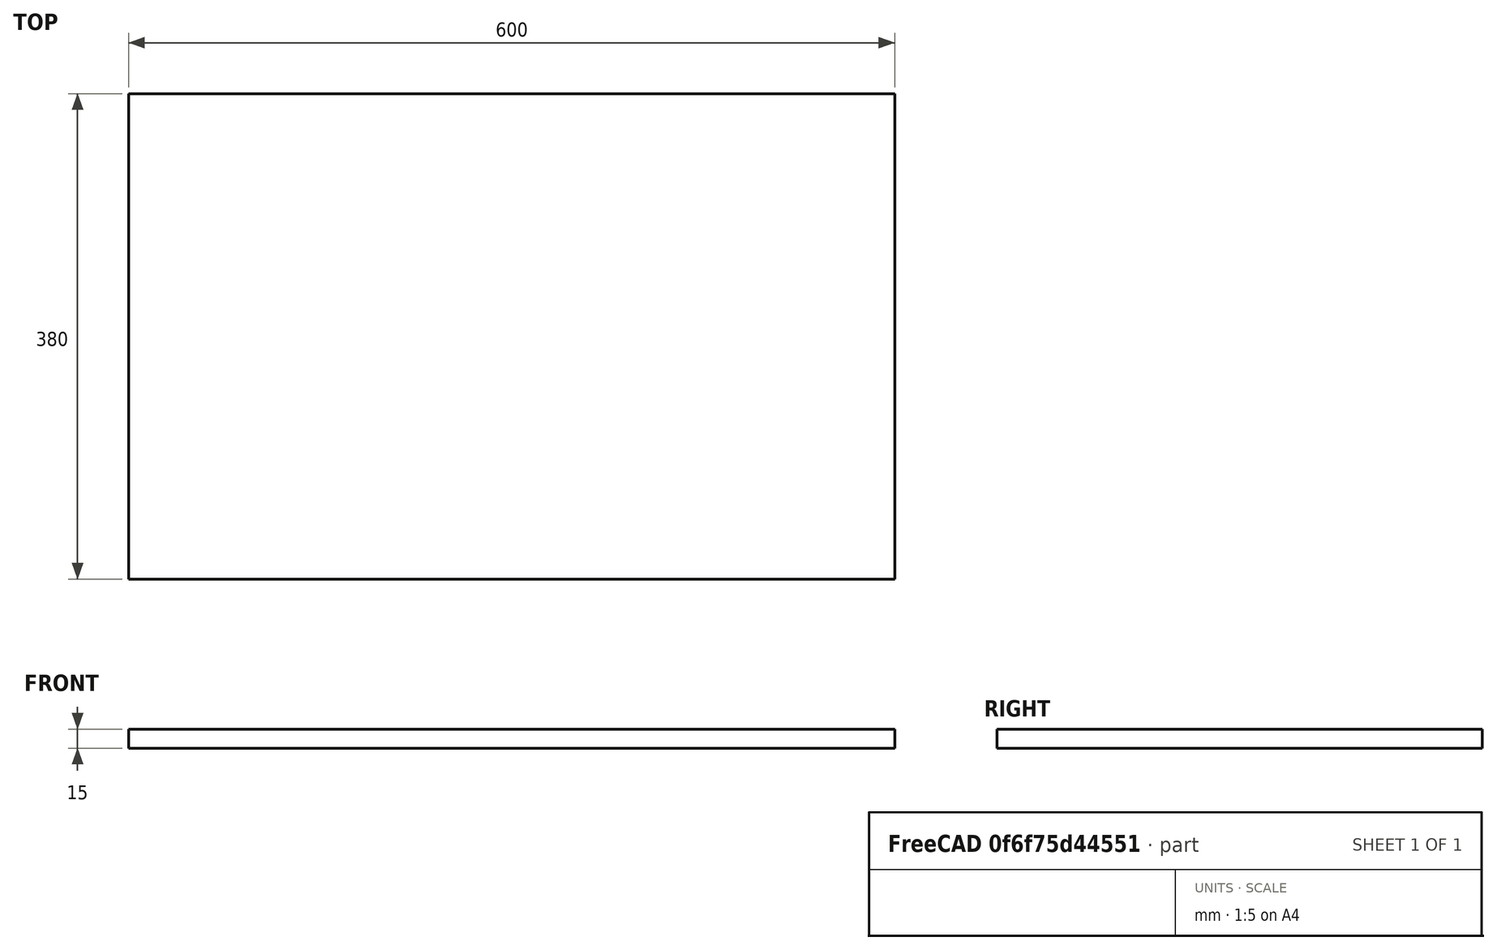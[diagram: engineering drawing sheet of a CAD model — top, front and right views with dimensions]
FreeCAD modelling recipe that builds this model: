
FCSTD DOCUMENT  (FreeCAD 1.0R39319 (Git))
Label: bottom
License: All rights reserved
LicenseURL: http://en.wikipedia.org/wiki/All_rights_reserved
objects: Sketcher::SketchObject×1, PartDesign::Pad×1, PartDesign::Body×1
note: 6 computed .brp shape members not serialized (recipe doc carries the construction recipe); baked Part::Feature solids carry a one-line shape summary decoded from their .brp

FEATURE [Sketcher::SketchObject] Sketch  label="bottom_sketch"
  ArcFitTolerance = 0
  AttachmentSupport = -> [XY_Plane]
  FullyConstrained = true
  MakeInternals = false
  MapMode = 5
  sketch-geometry (4):
    g0: LineSegment StartX=0 StartY=0 StartZ=0 EndX=600 EndY=0 EndZ=0
    g1: LineSegment StartX=600 StartY=0 StartZ=0 EndX=600 EndY=380 EndZ=0
    g2: LineSegment StartX=600 StartY=380 StartZ=0 EndX=0 EndY=380 EndZ=0
    g3: LineSegment StartX=0 StartY=380 StartZ=0 EndX=0 EndY=0 EndZ=0
  constraints (11):
    c: Coincident(g0,g1)
    c: Coincident(g1,g2)
    c: Coincident(g2,g3)
    c: Coincident(g3,g0)
    c: Horizontal(g0)
    c: Horizontal(g2)
    c: Vertical(g1)
    c: Vertical(g3)
    c: Coincident(g0,g-1)
    c: DistanceX(g0,g0) = 600
    c: DistanceY(g3,g3) = 380
FEATURE [PartDesign::Pad] Pad  label="bottom_pad"
  AllowMultiFace = false
  Direction = (0,0,1)
  Length = 15
  Length2 = 100
  Profile = -> Sketch
  ReferenceAxis = -> Sketch [N_Axis]
  Suppressed = false
  Type = 0
FEATURE [PartDesign::Body] Body  label="bottom_body"
  AllowCompound = false
  Group = -> [Sketch,Pad]
  Origin = -> Origin
  Tip = -> Pad
